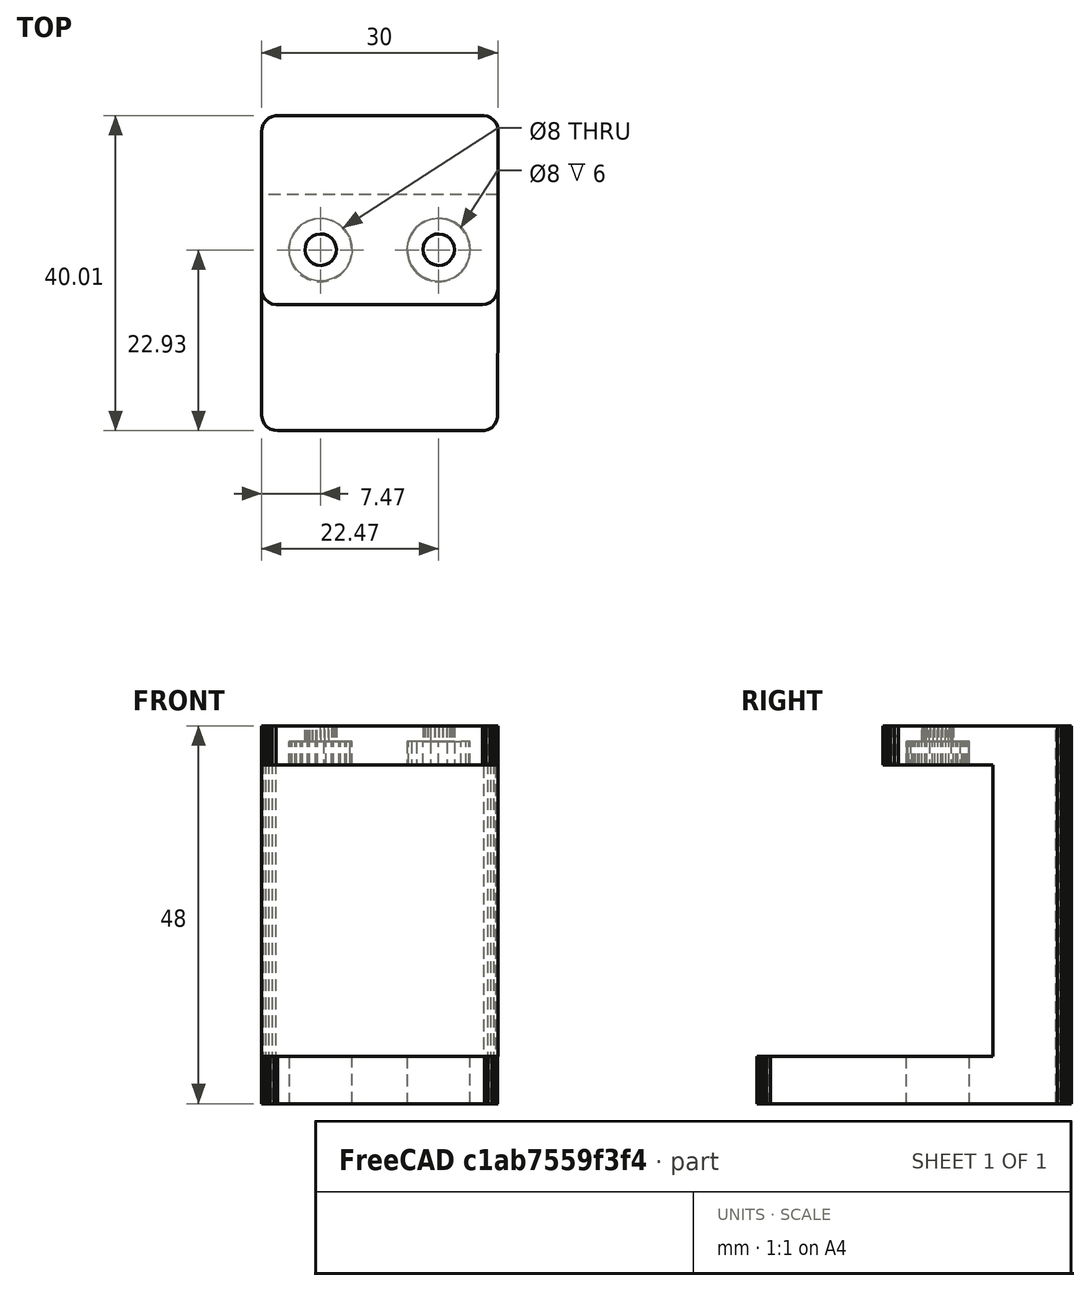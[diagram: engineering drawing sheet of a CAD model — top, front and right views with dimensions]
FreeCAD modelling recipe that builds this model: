
FCSTD DOCUMENT  (FreeCAD 0.21R33675 (Git))
Label: ifixit_wallmount_remix
License: All rights reserved
LicenseURL: https://en.wikipedia.org/wiki/All_rights_reserved
objects: Part::Cylinder×2, Part::Feature×2, Part::Cut×2, Mesh::Feature×1
note: 6 computed .brp shape members not serialized (recipe doc carries the construction recipe); baked Part::Feature solids carry a one-line shape summary decoded from their .brp

FEATURE [Part::Cylinder] Cylinder
  Angle = 360
  AttacherType = Attacher::AttachEngine3D
  FirstAngle = 0
  Height = 10
  Placement = pos=(9,23.5,-1) rot=(0,0,1;0rad)
  Radius = 4
  SecondAngle = 0
FEATURE [Part::Cylinder] Cylinder001
  Angle = 360
  AttacherType = Attacher::AttachEngine3D
  FirstAngle = 0
  Height = 10
  Placement = pos=(24,23.5,-1) rot=(0,0,1;0rad)
  Radius = 4
  SecondAngle = 0
FEATURE [Mesh::Feature] ifixit_wall_mount  label="ifixit-wall mount"
FEATURE [Part::Feature] ifixit_wall_mount001
  shape: bbox 30 x 40 x 48 mm, 562 faces, 0 solids (baked)
FEATURE [Part::Feature] ifixit_wall_mount001_solid  label="ifixit_wall_mount001 (Solid)"
  shape: bbox 30 x 40 x 48 mm, 562 faces (baked)
FEATURE [Part::Cut] Cut
  Base = -> ifixit_wall_mount001_solid
  Tool = -> Cylinder
FEATURE [Part::Cut] Cut001
  Base = -> Cut
  Tool = -> Cylinder001
